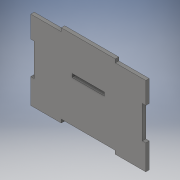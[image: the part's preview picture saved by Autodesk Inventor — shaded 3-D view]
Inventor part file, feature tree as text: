
AUTODESK INVENTOR PART (.ipt)
format: ipt  version: 2019 (Build 230136000, 136)  size: 138,752 bytes
history: native  units: mm
features: other x1, extrude x1, sketch x1
ambient origin geometry x8: Origin, YZ Plane, XZ Plane, XY Plane, X Axis, Y Axis, Z Axis, Center Point
bodies: Body1 (feature_tree)
feature tree (3):
  other  "Sólido1"
  extrude  "Extrusión1"  Depth=73.18mm
  sketch  "Boceto1"  dims[d0=106.36mm d3=73.18mm d4=3.18mm d5=50.0mm d6=25.0mm d8=30.0mm d9=30.0mm d10=3.18mm d11=20.0mm d12=20.0mm d13=50.0mm d14=25.0mm d17=30.0mm d18=3.18mm d19=40.0mm d20=15.0mm d21=3.18mm d22=0.0mm]
